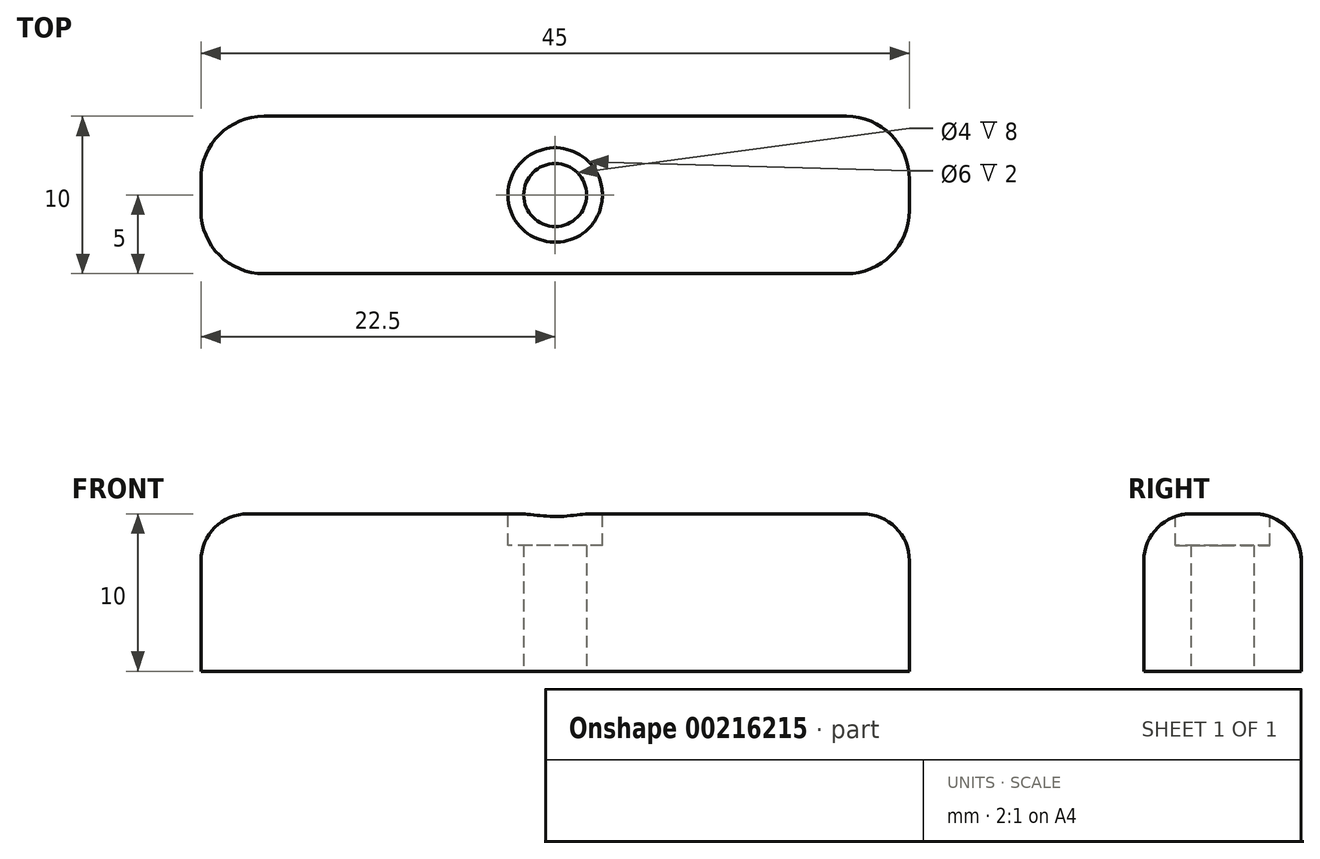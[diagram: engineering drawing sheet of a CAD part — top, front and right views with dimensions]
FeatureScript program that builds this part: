
annotation { "Feature Type Name" : "Feature", "Feature Type Description" : "" }
export const myFeature = defineFeature(function(context is Context, id is Id, definition is map)
    precondition{}
    {
        {
            var Q0;
            Q0=qCreatedBy(makeId("Top.planeOp"),FACE);
            var sketch = newSketch(context, id + "F0", { "sketchPlane" : qUnion([Q0])});
            skLineSegment(sketch, "E0.bottom", {"start": v(-22.5, 5) * mm, "end": v(22.5, 5) * mm});
            skLineSegment(sketch, "E0.top", {"start": v(-22.5, -5) * mm, "end": v(22.5, -5) * mm});
            skLineSegment(sketch, "E0.left", {"start": v(-22.5, 5) * mm, "end": v(-22.5, -5) * mm});
            skLineSegment(sketch, "E0.right", {"start": v(22.5, 5) * mm, "end": v(22.5, -5) * mm});
            skCircle(sketch, "E1", {"center": v(0, 0) * mm, "radius": 2 * mm});
            skCircle(sketch, "E2", {"center": v(0, 0) * mm, "radius": 3 * mm});
            skSolve(sketch);
        }
        {
            var Q0;
            Q0=makeQuery(id+"F0.imprint","IMPRINT",FACE,{"disambiguationData":[TD([[makeQuery(id+"F0.imprint","IMPRINT",EDGE,{"derivedFrom":sQuery(id+"F0.wireOp",EDGE,"E0.bottom")}),-1.0]])]});
            var Q1;
            Q1=makeQuery(id+"F0.imprint","IMPRINT",FACE,{"disambiguationData":[TD([[makeQuery(id+"F0.imprint","IMPRINT",EDGE,{"derivedFrom":sQuery(id+"F0.wireOp",EDGE,"E1")}),-1.0]])]});
            extrude(context, id + "F1", {"entities" : qUnion([Q0, Q1]), "depth" : 10 * mm});
        }
        {
            var Q0;
            Q0=makeQuery(id+"F1.opExtrude","SWEPT_EDGE",EDGE,{"disambiguationData":[OSD([sQuery(id+"F0.wireOp",EDGE,"E0.top"),sQuery(id+"F0.wireOp",EDGE,"E0.left")])]});
            var Q1;
            Q1=makeQuery(id+"F1.opExtrude","SWEPT_EDGE",EDGE,{"disambiguationData":[OSD([sQuery(id+"F0.wireOp",EDGE,"E0.top"),sQuery(id+"F0.wireOp",EDGE,"E0.right")])]});
            var Q2;
            Q2=makeQuery(id+"F1.opExtrude","SWEPT_EDGE",EDGE,{"disambiguationData":[OSD([sQuery(id+"F0.wireOp",EDGE,"E0.bottom"),sQuery(id+"F0.wireOp",EDGE,"E0.right")])]});
            var Q3;
            Q3=makeQuery(id+"F1.opExtrude","SWEPT_EDGE",EDGE,{"disambiguationData":[OSD([sQuery(id+"F0.wireOp",EDGE,"E0.bottom"),sQuery(id+"F0.wireOp",EDGE,"E0.left")])]});
            fillet(context, id + "F2", {"entities" : qUnion([Q0, Q1, Q2, Q3]), "radius" : 4 * mm, "tangentPropagation" : true, "allowEdgeOverflow" : false});
        }
        {
            var Q0;
            Q0=makeQuery(id+"F1.opExtrude","CAP_EDGE",EDGE,{"disambiguationData":[OSD([sQuery(id+"F0.wireOp",EDGE,"E0.top")])],"isStart":false});
            fillet(context, id + "F3", {"entities" : qUnion([Q0]), "radius" : 3 * mm, "tangentPropagation" : true, "allowEdgeOverflow" : false});
        }
        {
            var Q0;
            Q0=makeQuery(id+"F3.opFillet","SPLIT",FACE,{"disambiguationData":[OD(1.0)],"derivedFrom":makeQuery(id+"F1.opExtrude","CAP_FACE",FACE,{"disambiguationData":[OSD([sQuery(id+"F0.wireOp",EDGE,"E0.bottom"),sQuery(id+"F0.wireOp",EDGE,"E0.top"),sQuery(id+"F0.wireOp",EDGE,"E0.left"),sQuery(id+"F0.wireOp",EDGE,"E0.right"),sQuery(id+"F0.wireOp",EDGE,"E1")])],"isStart":false})});
            var sketch = newSketch(context, id + "F4", { "sketchPlane" : qUnion([Q0])});
            skCircle(sketch, "E3.0", {"center": v(0, 0) * mm, "radius": 2 * mm});
            skCircle(sketch, "E4.0", {"center": v(0, 0) * mm, "radius": 3 * mm});
            skSolve(sketch);
        }
        {
            var Q0;
            {var subQ0=sQuery(id+"F4.wireOp",EDGE,"E3.0");var subQ1=sQuery(id+"F0.wireOp",EDGE,"E0.top");var subQ2=sQuery(id+"F0.wireOp",EDGE,"E0.bottom");var subQ3=makeQuery(id+"F1.opExtrude","CAP_FACE",FACE,{"disambiguationData":[OSD([subQ2,subQ1,sQuery(id+"F0.wireOp",EDGE,"E0.left"),sQuery(id+"F0.wireOp",EDGE,"E0.right"),sQuery(id+"F0.wireOp",EDGE,"E1")])],"isStart":false});var subQ4=makeQuery(id+"F3.opFillet","BLEND_EDGE",EDGE,{"disambiguationData":[OD(0.0)],"blendedFrom":[makeQuery(id+"F1.opExtrude","CAP_EDGE",EDGE,{"disambiguationData":[OSD([subQ2])],"isStart":false}),subQ3],"blendedInto":[subQ3]});var subQ5=makeQuery(id+"F4.imprint","INTERSECT",VERTEX,{"derivedFrom":[subQ4,subQ0]});Q0=makeQuery(id+"F4.imprint","IMPRINT",FACE,{"disambiguationData":[TD([[makeQuery(id+"F4.imprint","IMPRINT",EDGE,{"disambiguationData":[TD([[subQ5,-1.0]])],"derivedFrom":subQ0}),-1.0]])]});}
            var Q1;
            {var subQ0=sQuery(id+"F4.wireOp",EDGE,"E3.0");var subQ1=sQuery(id+"F0.wireOp",EDGE,"E0.top");var subQ2=sQuery(id+"F0.wireOp",EDGE,"E0.bottom");var subQ3=makeQuery(id+"F1.opExtrude","CAP_FACE",FACE,{"disambiguationData":[OSD([subQ2,subQ1,sQuery(id+"F0.wireOp",EDGE,"E0.left"),sQuery(id+"F0.wireOp",EDGE,"E0.right"),sQuery(id+"F0.wireOp",EDGE,"E1")])],"isStart":false});var subQ4=makeQuery(id+"F3.opFillet","BLEND_EDGE",EDGE,{"disambiguationData":[OD(0.0)],"blendedFrom":[makeQuery(id+"F1.opExtrude","CAP_EDGE",EDGE,{"disambiguationData":[OSD([subQ2])],"isStart":false}),subQ3],"blendedInto":[subQ3]});var subQ5=makeQuery(id+"F4.imprint","INTERSECT",VERTEX,{"derivedFrom":[subQ4,subQ0]});Q1=makeQuery(id+"F4.imprint","IMPRINT",FACE,{"disambiguationData":[TD([[makeQuery(id+"F4.imprint","IMPRINT",EDGE,{"disambiguationData":[TD([[subQ5,1.0]])],"derivedFrom":subQ0}),-1.0]])]});}
            extrude(context, id + "F5", {"entities" : qUnion([Q0, Q1]), "operationType" : NewBodyOperationType.REMOVE, "oppositeDirection" : true, "depth" : 2 * mm});
        }
    });
